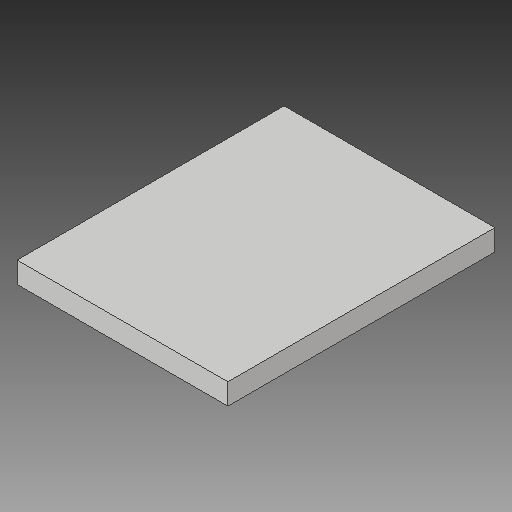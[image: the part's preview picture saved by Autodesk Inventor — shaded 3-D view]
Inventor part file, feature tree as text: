
AUTODESK INVENTOR PART (.ipt)
format: ipt  version: 2017 (Build 210142000, 142)  size: 76,800 bytes
history: native  units: in
note: dims shown in document units (in); Inventor stores cm internally (conversion verified against a paired STEP export)
features: extrude x1, sketch x1
ambient origin geometry x8: Origin, YZ Plane, XZ Plane, XY Plane, X Axis, Y Axis, Z Axis, Center Point
bodies: Solid1 (feature_tree)
feature tree (2):
  extrude  "Extrusion1"  Depth=9.5in
  sketch  "Sketch1"  dims[d0=7.5in d1=9.5in d2=0.75in d3=0.0in]
